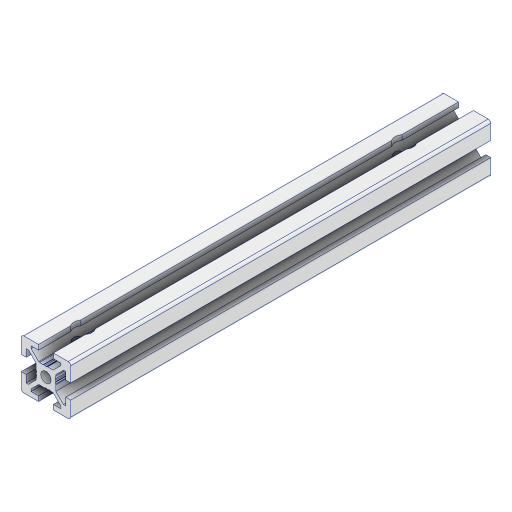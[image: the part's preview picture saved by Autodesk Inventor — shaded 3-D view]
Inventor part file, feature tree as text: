
AUTODESK INVENTOR PART (.ipt)
format: ipt  version: 2023 (Build 270158000, 158)  size: 343,552 bytes
history: native  units: mm
features: other x7, sketch x4, revolve x2, extrude x1, hole x1
ambient origin geometry x8: Origin, YZ Plane, XZ Plane, XY Plane, X Axis, Y Axis, Z Axis, Center Point
bodies: Solid1 (feature_tree)
feature tree (15):
  extrude  "Extrusion1"  TaperAngle=360.0deg  [1 undecoded]
  hole  "Hole1"  [1 undecoded]
  revolve  "Revolution1"  [1 undecoded]
  revolve  "Revolution2"  [1 undecoded]
  other  "C1_XY"
  other  "C1_YZ"
  other  "C1_ZX"
  other  "C1_X"
  other  "C1_Y"
  other  "C1_Z"
  other  "C1_Center"
  sketch  "Sketch_75"
  sketch  "Sketch2"  dims[d0=170.0mm d1=0.0mm]
  sketch  "Sketch_29"  dims[d2=4.2mm d3=6.0mm d4=4.0mm d5=2.0mm d6=90.0deg d7=170.0mm d8=0.0mm d9=360.0deg]
  sketch  "Sketch_32"  dims[d10=360.0deg d11=0.0mm]
note: 4 required parameter values undecoded (feature->parameter linkage not recoverable at this tier; creation-order binding heuristic only, values carry confidence <= 0.55)
